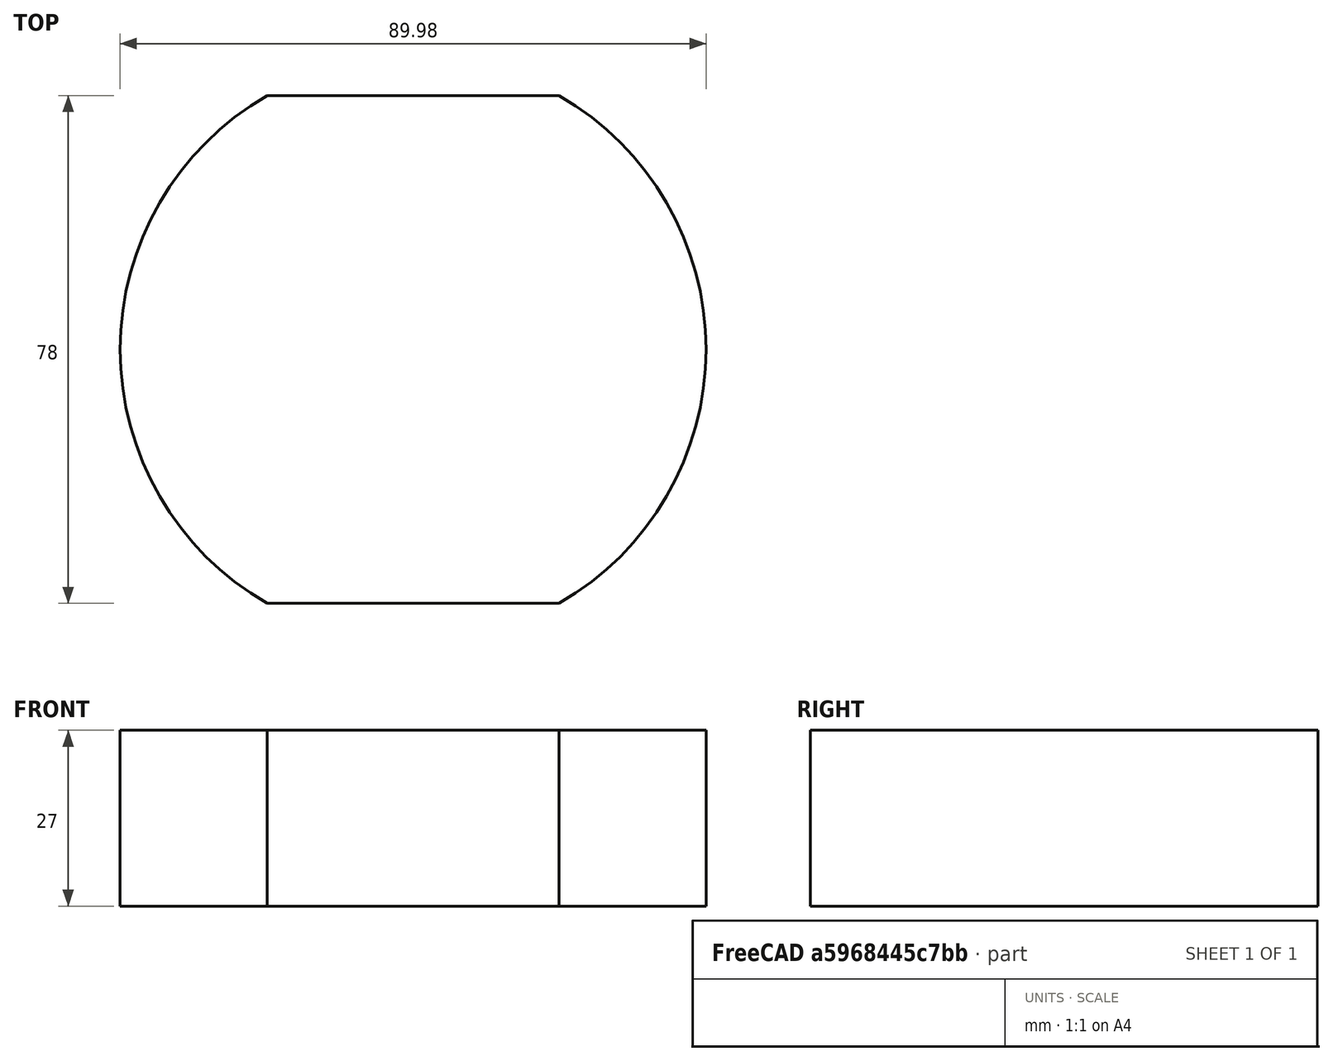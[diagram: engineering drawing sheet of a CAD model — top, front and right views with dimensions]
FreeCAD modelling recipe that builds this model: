
FCSTD DOCUMENT  (FreeCAD 1.0R39319 (Git))
Label: chapa_circle_90mm
License: All rights reserved
LicenseURL: https://en.wikipedia.org/wiki/All_rights_reserved
objects: Sketcher::SketchObject×1, PartDesign::Pad×1, PartDesign::Body×1
note: 6 computed .brp shape members not serialized (recipe doc carries the construction recipe); baked Part::Feature solids carry a one-line shape summary decoded from their .brp

FEATURE [Sketcher::SketchObject] Sketch_1
  ArcFitTolerance = 1e-06
  AttachmentSupport = -> [XY_Plane]
  FullyConstrained = false
  MakeInternals = false
  MapMode = 5
  sketch-geometry (4):
    g0: ArcOfCircle CenterX=0 CenterY=0.0103537 CenterZ=0 NormalX=0 NormalY=0 NormalZ=1 AngleXU=0 Radius=44.991 StartAngle=5.23436 EndAngle=7.33201
    g1: LineSegment StartX=22.4319 StartY=39.0104 StartZ=0 EndX=-22.4319 EndY=39.0104 EndZ=0
    g2: ArcOfCircle CenterX=0 CenterY=0.0103537 CenterZ=0 NormalX=0 NormalY=0 NormalZ=1 AngleXU=0 Radius=44.991 StartAngle=2.09276 EndAngle=4.19042
    g3: LineSegment StartX=-22.4319 StartY=-38.9896 StartZ=0 EndX=22.4319 EndY=-38.9896 EndZ=0
  constraints (7):
    c: Coincident(g0,g1)
    c: Coincident(g1,g2)
    c: Coincident(g2,g3)
    c: Coincident(g3,g0)
    c: Parallel(g1,g3)
    c: Horizontal(g1)
    c: Distance(g1,g3) = 78
FEATURE [PartDesign::Pad] Pad_1
  Direction = (0,0,1)
  Length = 27
  Length2 = 10
  Profile = -> Sketch_1
  Refine = true
  Suppressed = false
  Type = 0
FEATURE [PartDesign::Body] Body
  AllowCompound = false
  Group = -> [Sketch_1,Pad_1]
  Origin = -> Origin
  Tip = -> Pad_1
